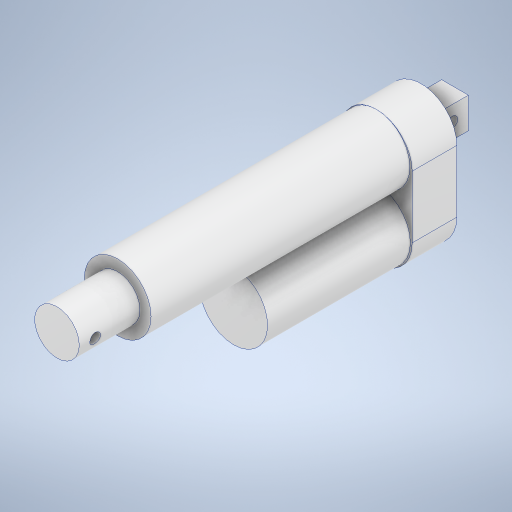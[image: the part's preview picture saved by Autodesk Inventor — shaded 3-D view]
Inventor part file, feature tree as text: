
AUTODESK INVENTOR PART (.ipt)
format: ipt  version: 2024 (Build 280153000, 153)  size: 304,128 bytes
history: native  units: mm
features: extrude x6, sketch x6, other x1
ambient origin geometry x8: Origin, YZ Plane, XZ Plane, XY Plane, X Axis, Y Axis, Z Axis, Center Point
bodies: Body1 (feature_tree)
feature tree (13):
  other  "솔리드1"
  extrude  "돌출1"  Depth=34.8mm
  extrude  "돌출2"  Depth=40.0mm
  extrude  "돌출3"  Depth=25.0mm TaperAngle=0.0deg
  extrude  "돌출4"  Depth=37.4mm
  extrude  "돌출5"  Depth=145.0mm TaperAngle=0.0deg
  extrude  "돌출6"  Depth=25.0mm
  sketch  "스케치1"
  sketch  "스케치2"
  sketch  "스케치3"
  sketch  "스케치5"
  sketch  "스케치6"
  sketch  "스케치7"
